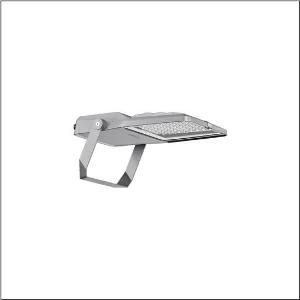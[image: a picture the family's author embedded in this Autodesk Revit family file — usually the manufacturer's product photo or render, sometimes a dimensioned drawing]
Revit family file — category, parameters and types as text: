
# Revit family: floodlight_fl_21_iq_mini___pl43_5xa7772d5a1a_690f
name_source: partatom
category: Lighting Fixtures
units: mm (PartAtom-declared; Revit-internal decimal feet)

## family parameters
Cut with Voids When Loaded = No
Host = Face
Light Source = No
Part Type = Normal
Room Calculation Point = No
Round Connector Dimension = Use Diameter
Shared = No

## types (1)
- --- (1 x LED, 17070 lm, 143 W, 4000K)
    Apparent Load = 143 VA
    CIE Flux Codes = 27 78 99 100 100
    Color Rendering = 80
    Color Temperature = 4000K
    Default Elevation = 1800 mm
    Description = Floodlight FL 21 iQ mini, floodlight, primary light control with lens, of PMMA, primary optical cover: protective disc, of toughened safety glass, transparent, light distribution: PL43, light emission: direct distribution, installation type: surface-mounted, LED, High Power LED, rated luminous flux: 17.070lm, luminous efficacy: 119lm/W, light colour: 840, colour temperature: 4000K, control: Street-Remote, Auto-Match, Temp-Guard, Night-Set, Smart-Wire, Desk-Remote (wireless, voltage-free reading and setting of iQ features in the workshop via application-optimized NFC function/RFID function), optimised constant luminous flux control (CLO 2.0), with terminal, 6-pole, mains connection: 220..240V, AC, 50/60Hz, start of lifetime: 143W, end of service life: 152W, reduction: 61W, luminaire housing, of diecast aluminium, powder-coated, Siteco® metallic grey (DB 702S), corrosivity category C5 mid according to DIN EN ISO 12944, sealing non-destructively replaceable, mounting bracket, of steel, galvanised, powder-coated, Siteco® metallic grey (DB 702S), protection rating (complete): IP66, insulation class (complete): insulation class II (safety insulation), certification: CE, ENEC, VDE, protection symbol: D, impact resistance: IK08, permissible operating ambient temperature: -40..+40°C, permissible operating ambient temperature for outdoor applications: -40..+50°C, standard: DIN EN 12944, LABS conformity tested according to VDMA 24364:2018-05, packaging unit: 1 piece

Light Distribution: PL43
    Height = 70 mm
    Lamp = 1 x LED
    Lamp Light Flux = 17070 lm
    Lamp Power = 143 W
    Lamp count = 1
    Length = 485 mm
    Luminous efficacy = 119 lm/W
    Manufacturer = Siteco
    ModVariant = No
    Model = 5XA7772D5A1A
    Number of Poles = 1
    OnlyDefault = Yes
    Power Factor = 1
    Product Name = Floodlight FL 21 iQ mini | PL43
    Product group = floodlight | pylon annexe
    ProductGroupID = 6200
    Protection Class = Protection class II
    Protection Degree = IP 66
    RLX_Detail_Level = 1
    RLX_Emergency_Light_Flux = 0 lm
    RLX_Emergency_Type = 0
    RLX_Emergency_Type_DB = No
    RlxData = <blob elided: 96201 chars, md5=478e1f32>
    Socket = socket
    Standby Power = 0 W
    System Light Flux = 17070 lm
    System Power = 143 W
    Type Comments = factory setting: luminous flux: 100 % | dim-lin: 254 | 730 mA
    Type Image = l_1006845.jpg
    URL = http://relux.com
    VarID = @adj_093735
    Voltage = 0 V
    Weight = 0.00 kg
    Width = 337 mm

## geometry (parser evidence)
native form markers: Blend x4, Sweep x11
no freeform markers — native parametric forms only
